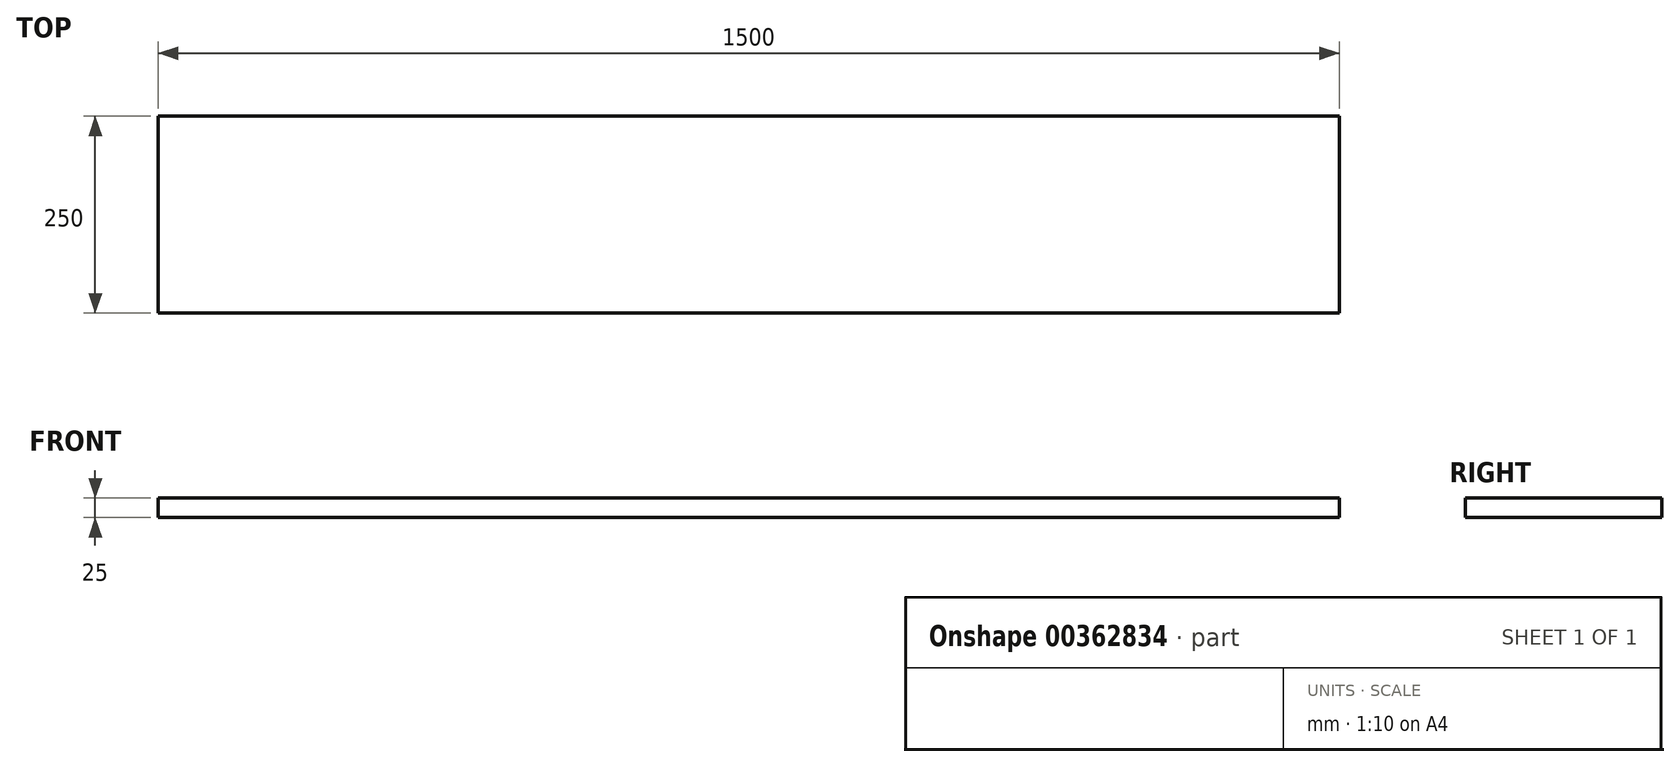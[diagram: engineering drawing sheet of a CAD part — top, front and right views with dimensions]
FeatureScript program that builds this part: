
annotation { "Feature Type Name" : "Feature", "Feature Type Description" : "" }
export const myFeature = defineFeature(function(context is Context, id is Id, definition is map)
    precondition{}
    {
        {
            var Q0;
            Q0=qCreatedBy(makeId("Top.planeOp"),FACE);
            var sketch = newSketch(context, id + "F0", { "sketchPlane" : qUnion([Q0])});
            skLineSegment(sketch, "E0.bottom", {"start": v(-750, 125) * mm, "end": v(750, 125) * mm});
            skLineSegment(sketch, "E0.top", {"start": v(-750, -125) * mm, "end": v(750, -125) * mm});
            skLineSegment(sketch, "E0.left", {"start": v(-750, 125) * mm, "end": v(-750, -125) * mm});
            skLineSegment(sketch, "E0.right", {"start": v(750, 125) * mm, "end": v(750, -125) * mm});
            skPoint(sketch, "E0.middle", {"position": v(0, 0) * mm});
            skLineSegment(sketch, "E1.bottom", {"start": v(-740, 115) * mm, "end": v(740, 115) * mm});
            skLineSegment(sketch, "E1.top", {"start": v(-740, -115) * mm, "end": v(740, -115) * mm});
            skLineSegment(sketch, "E1.left", {"start": v(-740, 115) * mm, "end": v(-740, -115) * mm});
            skLineSegment(sketch, "E1.right", {"start": v(740, 115) * mm, "end": v(740, -115) * mm});
            skSolve(sketch);
        }
        {
            var Q0;
            Q0=makeQuery(id+"F0.imprint","IMPRINT",FACE,{"disambiguationData":[TD([[makeQuery(id+"F0.imprint","IMPRINT",EDGE,{"derivedFrom":sQuery(id+"F0.wireOp",EDGE,"E0.bottom")}),-1.0]])]});
            var Q1;
            Q1=makeQuery(id+"F0.imprint","IMPRINT",FACE,{"disambiguationData":[TD([[makeQuery(id+"F0.imprint","IMPRINT",EDGE,{"derivedFrom":sQuery(id+"F0.wireOp",EDGE,"E1.bottom")}),-1.0]])]});
            extrude(context, id + "F1", {"entities" : qUnion([Q0, Q1]), "depth" : 25 * mm});
        }
    });
